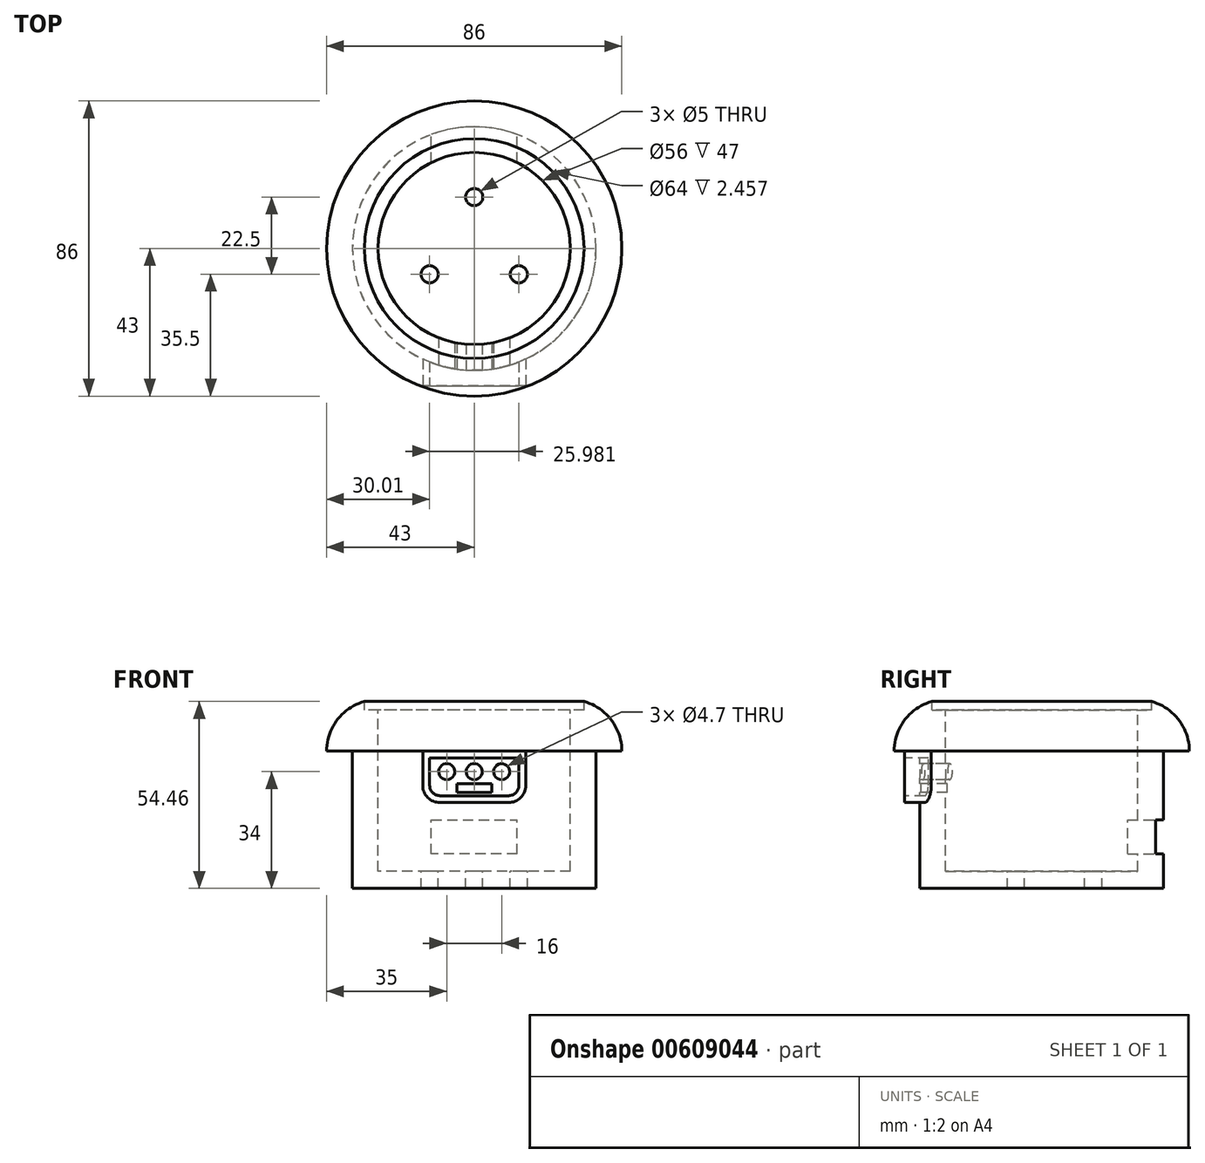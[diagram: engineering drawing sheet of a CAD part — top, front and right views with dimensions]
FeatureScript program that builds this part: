
annotation { "Feature Type Name" : "Feature", "Feature Type Description" : "" }
export const myFeature = defineFeature(function(context is Context, id is Id, definition is map)
    precondition{}
    {
        {
            var Q0;
            Q0=qCreatedBy(makeId("Front.planeOp"),FACE);
            var sketch = newSketch(context, id + "F0", { "sketchPlane" : qUnion([Q0])});
            skLineSegment(sketch, "E0", {"start": v(43, 30) * mm, "end": v(43, 15) * mm});
            skLineSegment(sketch, "E1", {"start": v(43, 15) * mm, "end": v(35.5, 15) * mm});
            skLineSegment(sketch, "E2", {"start": v(35.5, 15) * mm, "end": v(35.5, -15) * mm});
            skLineSegment(sketch, "E3", {"start": v(43, 30) * mm, "end": v(28, 30) * mm});
            skLineSegment(sketch, "E4", {"start": v(28, 30) * mm, "end": v(28, -20) * mm});
            skLineSegment(sketch, "E5", {"start": v(28, -20) * mm, "end": v(0, -20) * mm});
            skLineSegment(sketch, "E6", {"start": v(0, -25) * mm, "end": v(35.5, -25) * mm});
            skLineSegment(sketch, "E7", {"start": v(35.5, -25) * mm, "end": v(35.5, -15) * mm});
            skLineSegment(sketch, "E8", {"start": v(0, -20) * mm, "end": v(0, -25) * mm});
            skSolve(sketch);
        }
        {
            var Q0;
            Q0=makeQuery(id+"F0.imprint","IMPRINT",FACE,{"disambiguationData":[TD([[makeQuery(id+"F0.imprint","IMPRINT",EDGE,{"derivedFrom":sQuery(id+"F0.wireOp",EDGE,"E0")}),-1.0]])]});
            var Q1;
            Q1=sQuery(id+"F0.wireOp",EDGE,"E8");
            revolve(context, id + "F1", {"entities" : qUnion([Q0]), "axis" : qUnion([Q1]), "revolveType" : RevolveType.FULL});
        }
        {
            var Q0;
            Q0=makeQuery(id+"F1.opRevolve","SWEPT_EDGE",EDGE,{"disambiguationData":[OSD([sQuery(id+"F0.wireOp",EDGE,"E0"),sQuery(id+"F0.wireOp",EDGE,"E3")])]});
            fillet(context, id + "F2", {"entities" : qUnion([Q0]), "radius" : 15 * mm, "tangentPropagation" : true, "allowEdgeOverflow" : false});
        }
        {
            var Q0;
            Q0=makeQuery(id+"F1.opRevolve","SWEPT_FACE",FACE,{"disambiguationData":[OSD([sQuery(id+"F0.wireOp",EDGE,"E5")])]});
            var sketch = newSketch(context, id + "F3", { "sketchPlane" : qUnion([Q0])});
            skPoint(sketch, "E9", {"position": v(0, 15) * mm});
            skPoint(sketch, "E10.1.0", {"position": v(-13, -7.5) * mm});
            skPoint(sketch, "E10.2.0", {"position": v(13, -7.5) * mm});
            skPoint(sketch, "E10.center", {"position": v(0, 0) * mm});
            skSolve(sketch);
        }
        {
            var Q0;
            Q0=sQuery(id+"F3.wireOp",VERTEX,"E9");
            var Q1;
            Q1=sQuery(id+"F3.wireOp",VERTEX,"E10.1.0");
            var Q2;
            Q2=sQuery(id+"F3.wireOp",VERTEX,"E10.2.0");
            var Q3;
            Q3=makeQuery(id+"F1.opRevolve","SWEPT_BODY",BODY,{"disambiguationData":[OSD([sQuery(id+"F0.wireOp",EDGE,"E0"),sQuery(id+"F0.wireOp",EDGE,"E1"),sQuery(id+"F0.wireOp",EDGE,"E2"),sQuery(id+"F0.wireOp",EDGE,"E3"),sQuery(id+"F0.wireOp",EDGE,"E4"),sQuery(id+"F0.wireOp",EDGE,"E5"),sQuery(id+"F0.wireOp",EDGE,"E6"),sQuery(id+"F0.wireOp",EDGE,"E7"),sQuery(id+"F0.wireOp",EDGE,"E8")])]});
            hole(context, id + "F4", {"style" : HoleStyle.SIMPLE, "endStyle" : HoleEndStyle.THROUGH, "holeDiameter" : 5 * mm, "majorDiameter" : 5 * mm, "isTappedThrough" : true, "tappedDepth" : 12 * mm, "tapClearance" : 3, "locations" : qUnion([Q0, Q1, Q2]), "scope" : qUnion([Q3])});
        }
        {
            var Q0;
            Q0=qCreatedBy(makeId("Top.planeOp"),FACE);
            cPlane(context, id + "F5", {"entities" : qUnion([Q0]), "cplaneType" : CPlaneType.OFFSET, "offset" : 30 * mm, "width" : 150 * mm, "height" : 150 * mm});
        }
        {
            var Q0;
            Q0=qCreatedBy(id+"F5.planeOp",FACE);
            var sketch = newSketch(context, id + "F6", { "sketchPlane" : qUnion([Q0])});
            skLineSegment(sketch, "E11", {"start": v(0, 0) * mm, "end": v(32, 0) * mm});
            skCircle(sketch, "E12", {"center": v(0, 0) * mm, "radius": 32 * mm});
            skSolve(sketch);
        }
        {
            var Q0;
            Q0=makeQuery(id+"F6.imprint","IMPRINT",FACE,{"disambiguationData":[TD([[makeQuery(id+"F6.imprint","IMPRINT",EDGE,{"derivedFrom":sQuery(id+"F6.wireOp",EDGE,"E12")}),1.0]])]});
            extrude(context, id + "F7", {"entities" : qUnion([Q0]), "operationType" : NewBodyOperationType.REMOVE, "oppositeDirection" : true, "depth" : 3 * mm, "offsetDistance" : 25 * mm});
        }
        {
            var Q0;
            Q0=makeQuery(id+"F7.boolean.opBoolean","COPY",FACE,{"derivedFrom":makeQuery(id+"F7.opExtrude","CAP_FACE",FACE,{"disambiguationData":[OSD([sQuery(id+"F0.wireOp",EDGE,"E3"),sQuery(id+"F0.wireOp",EDGE,"E4"),sQuery(id+"F6.wireOp",EDGE,"E12")])],"isStart":false})});
            var sketch = newSketch(context, id + "F8", { "sketchPlane" : qUnion([Q0])});
            skPoint(sketch, "E13", {"position": v(0, 0) * mm});
            skSolve(sketch);
        }
        {
            var Q0;
            Q0=qCreatedBy(makeId("Front.planeOp"),FACE);
            cPlane(context, id + "F9", {"entities" : qUnion([Q0]), "cplaneType" : CPlaneType.OFFSET, "offset" : 40 * mm, "width" : 150 * mm, "height" : 150 * mm});
        }
        {
            var Q0;
            Q0=qCreatedBy(id+"F9.planeOp",FACE);
            var sketch = newSketch(context, id + "F10", { "sketchPlane" : qUnion([Q0])});
            skLineSegment(sketch, "E14", {"start": v(0, 0) * mm, "end": v(15, 0) * mm});
            skLineSegment(sketch, "E15", {"start": v(15, 0) * mm, "end": v(15, 15) * mm});
            skLineSegment(sketch, "E16", {"start": v(15, 15) * mm, "end": v(-15, 15) * mm});
            skLineSegment(sketch, "E17", {"start": v(-15, 15) * mm, "end": v(-15, 0) * mm});
            skLineSegment(sketch, "E18", {"start": v(-15, 0) * mm, "end": v(0, 0) * mm});
            skLineSegment(sketch, "E19", {"start": v(0, 0) * mm, "end": v(0, 2) * mm});
            skLineSegment(sketch, "E20", {"start": v(0, 2) * mm, "end": v(-13, 2) * mm});
            skLineSegment(sketch, "E21", {"start": v(-13, 2) * mm, "end": v(-13, 13) * mm});
            skLineSegment(sketch, "E22", {"start": v(-13, 13) * mm, "end": v(13, 13) * mm});
            skLineSegment(sketch, "E23", {"start": v(13, 13) * mm, "end": v(13, 2) * mm});
            skLineSegment(sketch, "E24", {"start": v(13, 2) * mm, "end": v(0, 2) * mm});
            skLineSegment(sketch, "E25", {"start": v(0, 2) * mm, "end": v(0, 5) * mm});
            skLineSegment(sketch, "E26", {"start": v(0, 5) * mm, "end": v(0, 9) * mm});
            skLineSegment(sketch, "E27", {"start": v(0, 9) * mm, "end": v(8, 9) * mm});
            skLineSegment(sketch, "E28", {"start": v(8, 9) * mm, "end": v(0, 9) * mm});
            skLineSegment(sketch, "E29", {"start": v(0, 9) * mm, "end": v(-8, 9) * mm});
            skSolve(sketch);
        }
        {
            var Q0;
            Q0=qSketchRegion(id+"F10",true);
            extrude(context, id + "F11", {"entities" : qUnion([Q0]), "operationType" : NewBodyOperationType.ADD, "oppositeDirection" : true, "depth" : 25 * mm, "offsetDistance" : 25 * mm});
        }
        {
            var Q0;
            Q0=makeQuery(id+"F8.imprint","IMPRINT",FACE,{"disambiguationData":[TD([[makeQuery(id+"F8.imprint","IMPRINT",EDGE,{"derivedFrom":makeQuery(id+"F7.boolean.opBoolean","INTERSECT",EDGE,{"derivedFrom":[makeQuery(id+"F1.opRevolve","SWEPT_FACE",FACE,{"disambiguationData":[OSD([sQuery(id+"F0.wireOp",EDGE,"E4")])]}),makeQuery(id+"F7.opExtrude","CAP_FACE",FACE,{"disambiguationData":[OSD([sQuery(id+"F6.wireOp",EDGE,"E12")])],"isStart":false})]})}),-1.0]])]});
            extrude(context, id + "F12", {"entities" : qUnion([Q0]), "operationType" : NewBodyOperationType.REMOVE, "oppositeDirection" : true, "depth" : 40 * mm, "offsetDistance" : 25 * mm});
        }
        {
            var Q0;
            {var subQ0=sQuery(id+"F10.wireOp",EDGE,"E18");var subQ1=sQuery(id+"F10.wireOp",EDGE,"E17");Q0=makeQuery(id+"F11.boolean.opBoolean","SPLIT",EDGE,{"disambiguationData":[TD([makeQuery(id+"F1.opRevolve","SWEPT_FACE",FACE,{"disambiguationData":[OSD([sQuery(id+"F0.wireOp",EDGE,"E2"),sQuery(id+"F0.wireOp",EDGE,"E7")])]})])],"derivedFrom":makeQuery(id+"F11.opExtrude","SWEPT_EDGE",EDGE,{"disambiguationData":[OSD([subQ1,subQ0])]})});}
            var Q1;
            {var subQ1=sQuery(id+"F10.wireOp",EDGE,"E15");var subQ2=sQuery(id+"F10.wireOp",EDGE,"E14");Q1=makeQuery(id+"F11.boolean.opBoolean","SPLIT",EDGE,{"disambiguationData":[TD([makeQuery(id+"F1.opRevolve","SWEPT_FACE",FACE,{"disambiguationData":[OSD([sQuery(id+"F0.wireOp",EDGE,"E2"),sQuery(id+"F0.wireOp",EDGE,"E7")])]})])],"derivedFrom":makeQuery(id+"F11.opExtrude","SWEPT_EDGE",EDGE,{"disambiguationData":[OSD([subQ2,subQ1])]})});}
            fillet(context, id + "F13", {"entities" : qUnion([Q0, Q1]), "radius" : 5 * mm, "tangentPropagation" : true, "allowEdgeOverflow" : false});
        }
        {
            var Q0;
            {var subQ1=sQuery(id+"F10.wireOp",EDGE,"E21");var subQ2=sQuery(id+"F10.wireOp",EDGE,"E20");Q0=makeQuery(id+"F11.boolean.opBoolean","SPLIT",EDGE,{"disambiguationData":[TD([makeQuery(id+"F1.opRevolve","SWEPT_FACE",FACE,{"disambiguationData":[OSD([sQuery(id+"F0.wireOp",EDGE,"E2"),sQuery(id+"F0.wireOp",EDGE,"E7")])]})])],"derivedFrom":makeQuery(id+"F11.opExtrude","SWEPT_EDGE",EDGE,{"disambiguationData":[OSD([subQ2,subQ1])]})});}
            var Q1;
            {var subQ0=sQuery(id+"F10.wireOp",EDGE,"E23");var subQ1=sQuery(id+"F10.wireOp",EDGE,"E24");Q1=makeQuery(id+"F11.boolean.opBoolean","SPLIT",EDGE,{"disambiguationData":[TD([makeQuery(id+"F1.opRevolve","SWEPT_FACE",FACE,{"disambiguationData":[OSD([sQuery(id+"F0.wireOp",EDGE,"E2"),sQuery(id+"F0.wireOp",EDGE,"E7")])]})])],"derivedFrom":makeQuery(id+"F11.opExtrude","SWEPT_EDGE",EDGE,{"disambiguationData":[OSD([subQ0,subQ1])]})});}
            fillet(context, id + "F14", {"entities" : qUnion([Q0, Q1]), "radius" : 3 * mm, "tangentPropagation" : true, "allowEdgeOverflow" : false});
        }
        {
            var Q0;
            Q0=sQuery(id+"F10.wireOp",VERTEX,"E29.end");
            var Q1;
            Q1=sQuery(id+"F10.wireOp",VERTEX,"E28.end");
            var Q2;
            Q2=sQuery(id+"F10.wireOp",VERTEX,"E28.start");
            var Q3;
            Q3=makeQuery(id+"F1.opRevolve","SWEPT_BODY",BODY,{"disambiguationData":[OSD([sQuery(id+"F0.wireOp",EDGE,"E0"),sQuery(id+"F0.wireOp",EDGE,"E1"),sQuery(id+"F0.wireOp",EDGE,"E2"),sQuery(id+"F0.wireOp",EDGE,"E3"),sQuery(id+"F0.wireOp",EDGE,"E4"),sQuery(id+"F0.wireOp",EDGE,"E5"),sQuery(id+"F0.wireOp",EDGE,"E6"),sQuery(id+"F0.wireOp",EDGE,"E7"),sQuery(id+"F0.wireOp",EDGE,"E8")])]});
            hole(context, id + "F15", {"style" : HoleStyle.SIMPLE, "endStyle" : HoleEndStyle.BLIND, "holeDiameter" : 4.7 * mm, "majorDiameter" : 5 * mm, "holeDepth" : 12 * mm, "isTappedThrough" : true, "tappedDepth" : 12 * mm, "tapClearance" : 3, "locations" : qUnion([Q0, Q1, Q2]), "scope" : qUnion([Q3])});
        }
        {
            var Q0;
            Q0=qCreatedBy(makeId("Front.planeOp"),FACE);
            cPlane(context, id + "F16", {"entities" : qUnion([Q0]), "cplaneType" : CPlaneType.OFFSET, "offset" : 36 * mm, "oppositeDirection" : true, "width" : 150 * mm, "height" : 150 * mm});
        }
        {
            var Q0;
            Q0=qCreatedBy(id+"F16.planeOp",FACE);
            var sketch = newSketch(context, id + "F17", { "sketchPlane" : qUnion([Q0])});
            skLineSegment(sketch, "E30", {"start": v(0, 0) * mm, "end": v(0, -15) * mm});
            skLineSegment(sketch, "E31", {"start": v(0, -15) * mm, "end": v(12.5, -15) * mm});
            skLineSegment(sketch, "E32.bottom", {"start": v(12.5, -15) * mm, "end": v(-12.5, -15) * mm});
            skLineSegment(sketch, "E32.top", {"start": v(12.5, -5) * mm, "end": v(-12.5, -5) * mm});
            skLineSegment(sketch, "E32.left", {"start": v(12.5, -15) * mm, "end": v(12.5, -5) * mm});
            skLineSegment(sketch, "E32.right", {"start": v(-12.5, -15) * mm, "end": v(-12.5, -5) * mm});
            skSolve(sketch);
        }
        {
            var Q0;
            {var subQ5=sQuery(id+"F17.wireOp",EDGE,"E32.left");Q0=makeQuery(id+"F17.imprint","IMPRINT",FACE,{"disambiguationData":[TD([[makeQuery(id+"F17.imprint","IMPRINT",EDGE,{"derivedFrom":subQ5}),1.0]])]});}
            var Q1;
            {var subQ5=sQuery(id+"F17.wireOp",EDGE,"E32.right");Q1=makeQuery(id+"F17.imprint","IMPRINT",FACE,{"disambiguationData":[TD([[makeQuery(id+"F17.imprint","IMPRINT",EDGE,{"derivedFrom":subQ5}),-1.0]])]});}
            extrude(context, id + "F18", {"entities" : qUnion([Q0, Q1]), "operationType" : NewBodyOperationType.REMOVE, "depth" : 25 * mm, "offsetDistance" : 25 * mm});
        }
        {
            var Q0;
            Q0=makeQuery(id+"F10.imprint","IMPRINT",FACE,{"disambiguationData":[TD([[makeQuery(id+"F10.imprint","IMPRINT",EDGE,{"derivedFrom":sQuery(id+"F10.wireOp",EDGE,"E14")}),1.0]])]});
            var sketch = newSketch(context, id + "F19", { "sketchPlane" : qUnion([Q0])});
            skLineSegment(sketch, "E33", {"start": v(0, 0) * mm, "end": v(0, 3) * mm});
            skLineSegment(sketch, "E34", {"start": v(0, 3) * mm, "end": v(5.1, 3) * mm});
            skLineSegment(sketch, "E35", {"start": v(5.1, 3) * mm, "end": v(5.1, 5.54) * mm});
            skLineSegment(sketch, "E36", {"start": v(5.1, 5.54) * mm, "end": v(-5.1, 5.54) * mm});
            skLineSegment(sketch, "E37", {"start": v(-5.1, 5.54) * mm, "end": v(-5.1, 3) * mm});
            skLineSegment(sketch, "E38", {"start": v(-5.1, 3) * mm, "end": v(0, 3) * mm});
            skSolve(sketch);
        }
        {
            var Q0;
            Q0=qSketchRegion(id+"F19",true);
            extrude(context, id + "F20", {"entities" : qUnion([Q0]), "operationType" : NewBodyOperationType.REMOVE, "oppositeDirection" : true, "depth" : 25 * mm, "offsetDistance" : 25 * mm});
        }
    });
